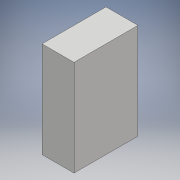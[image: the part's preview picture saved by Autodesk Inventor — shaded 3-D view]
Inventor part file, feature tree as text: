
AUTODESK INVENTOR PART (.ipt)
format: ipt  version: 2017 (Build 210142000, 142)  size: 228,864 bytes
history: native  units: mm
features: extrude x3, sketch x3, other x1
ambient origin geometry x8: Origin, YZ Plane, XZ Plane, XY Plane, X Axis, Y Axis, Z Axis, Center Point
bodies: Body1 (feature_tree)
feature tree (7):
  other  "Твердое тело1"
  extrude  "Выдавливание1"  Depth=10.0mm
  sketch  "Эскиз2"
  extrude  "Выдавливание2"  Depth=30.0mm
  extrude  "Выдавливание3"  Depth=20.0mm TaperAngle=0.0deg
  sketch  "Эскиз1"
  sketch  "Эскиз3"
